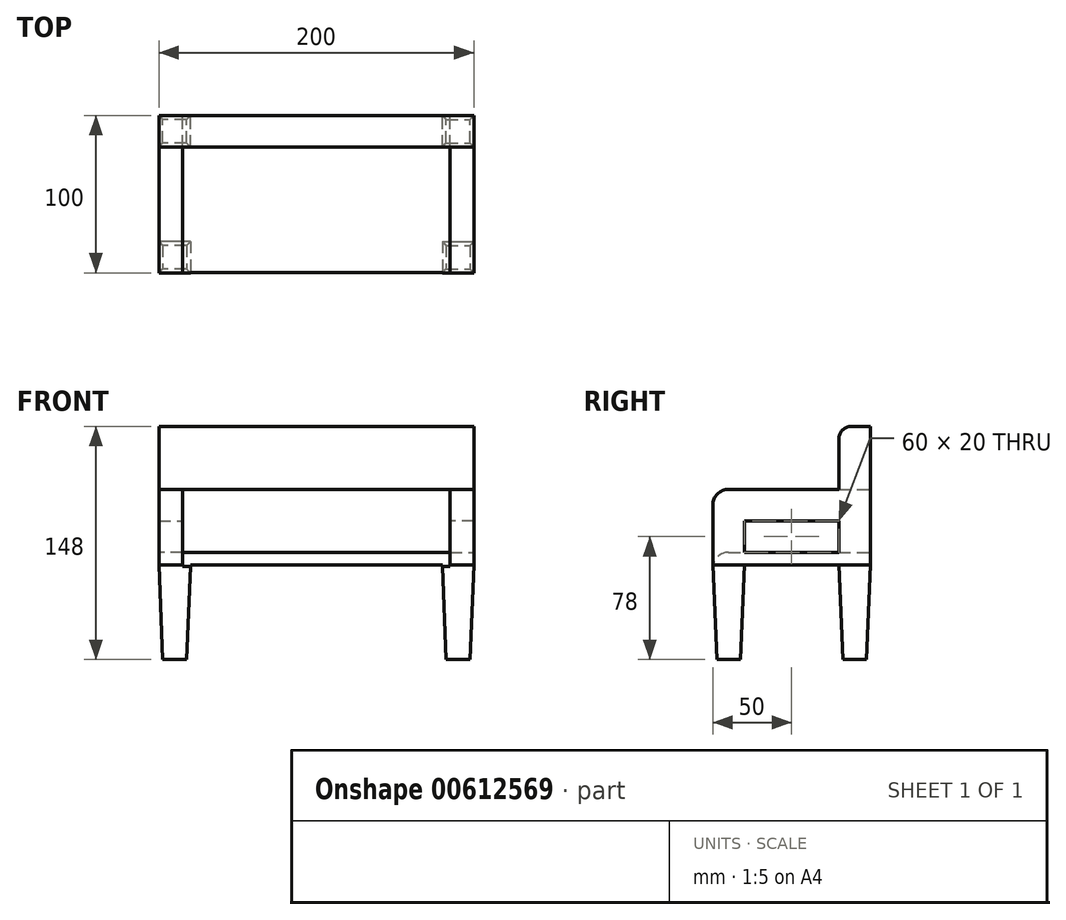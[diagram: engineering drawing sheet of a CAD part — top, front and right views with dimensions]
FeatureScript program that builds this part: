
annotation { "Feature Type Name" : "Feature", "Feature Type Description" : "" }
export const myFeature = defineFeature(function(context is Context, id is Id, definition is map)
    precondition{}
    {
        {
            var Q0;
            Q0=qCreatedBy(makeId("Top.planeOp"),FACE);
            var sketch = newSketch(context, id + "F0", { "sketchPlane" : qUnion([Q0])});
            skLineSegment(sketch, "E0.bottom", {"start": v(100, -50) * mm, "end": v(-100, -50) * mm});
            skLineSegment(sketch, "E0.top", {"start": v(100, 50) * mm, "end": v(-100, 50) * mm});
            skLineSegment(sketch, "E0.left", {"start": v(100, -50) * mm, "end": v(100, 50) * mm});
            skLineSegment(sketch, "E0.right", {"start": v(-100, -50) * mm, "end": v(-100, 50) * mm});
            skPoint(sketch, "E0.middle", {"position": v(0, 0) * mm});
            skSolve(sketch);
        }
        {
            var Q0;
            Q0=makeQuery(id+"F0.imprint","IMPRINT",FACE,{"disambiguationData":[TD([[makeQuery(id+"F0.imprint","IMPRINT",EDGE,{"derivedFrom":sQuery(id+"F0.wireOp",EDGE,"E0.bottom")}),-1.0]])]});
            extrude(context, id + "F1", {"entities" : qUnion([Q0]), "depth" : 8 * mm, "offsetDistance" : 25 * mm});
        }
        {
            var Q0;
            Q0=makeQuery(id+"F1.opExtrude","CAP_FACE",FACE,{"disambiguationData":[OSD([sQuery(id+"F0.wireOp",EDGE,"E0.bottom"),sQuery(id+"F0.wireOp",EDGE,"E0.top"),sQuery(id+"F0.wireOp",EDGE,"E0.left"),sQuery(id+"F0.wireOp",EDGE,"E0.right")])],"isStart":true});
            var sketch = newSketch(context, id + "F2", { "sketchPlane" : qUnion([Q0])});
            skPoint(sketch, "E1.middle", {"position": v(0, 0) * mm});
            skLineSegment(sketch, "E2.bottom", {"start": v(-80, 30) * mm, "end": v(-100, 30) * mm});
            skLineSegment(sketch, "E2.top", {"start": v(-80, 50) * mm, "end": v(-100, 50) * mm});
            skLineSegment(sketch, "E2.left", {"start": v(-80, 30) * mm, "end": v(-80, 50) * mm});
            skLineSegment(sketch, "E2.right", {"start": v(-100, 30) * mm, "end": v(-100, 50) * mm});
            skPoint(sketch, "E2.middle", {"position": v(-90, 40) * mm});
            skSolve(sketch);
        }
        {
            var Q0;
            Q0=qCreatedBy(makeId("Top.planeOp"),FACE);
            cPlane(context, id + "F3", {"entities" : qUnion([Q0]), "cplaneType" : CPlaneType.OFFSET, "offset" : 60 * mm, "oppositeDirection" : true, "width" : 150 * mm, "height" : 150 * mm});
        }
        {
            var Q0;
            Q0=qCreatedBy(id+"F3.planeOp",FACE);
            var sketch = newSketch(context, id + "F4", { "sketchPlane" : qUnion([Q0])});
            skLineSegment(sketch, "E3.bottom", {"start": v(-82.5, -32.5) * mm, "end": v(-97.5, -32.5) * mm});
            skLineSegment(sketch, "E3.top", {"start": v(-82.5, -47.5) * mm, "end": v(-97.5, -47.5) * mm});
            skLineSegment(sketch, "E3.left", {"start": v(-82.5, -32.5) * mm, "end": v(-82.5, -47.5) * mm});
            skLineSegment(sketch, "E3.right", {"start": v(-97.5, -32.5) * mm, "end": v(-97.5, -47.5) * mm});
            skPoint(sketch, "E3.middle", {"position": v(-90, -40) * mm});
            skSolve(sketch);
        }
        {
            var Q1;
            Q1=makeQuery(id+"F2.imprint","IMPRINT",FACE,{"disambiguationData":[TD([[makeQuery(id+"F2.imprint","IMPRINT",EDGE,{"derivedFrom":sQuery(id+"F2.wireOp",EDGE,"E2.bottom")}),-1.0]])]});
            var Q2;
            Q2=makeQuery(id+"F4.imprint","IMPRINT",FACE,{"disambiguationData":[TD([[makeQuery(id+"F4.imprint","IMPRINT",EDGE,{"derivedFrom":sQuery(id+"F4.wireOp",EDGE,"E3.bottom")}),1.0]])]});
            loft(context, id + "F5", {"operationType" : NewBodyOperationType.ADD, "sheetProfilesArray" : [{ "sheetProfileEntities" : qUnion([Q1]) }, { "sheetProfileEntities" : qUnion([Q2]) }]});
        }
        {
            var Q0;
            Q0=makeQuery(id+"F1.opExtrude","SWEPT_BODY",BODY,{"disambiguationData":[OSD([sQuery(id+"F0.wireOp",EDGE,"E0.bottom"),sQuery(id+"F0.wireOp",EDGE,"E0.top"),sQuery(id+"F0.wireOp",EDGE,"E0.left"),sQuery(id+"F0.wireOp",EDGE,"E0.right")])]});
            var Q1;
            Q1=qCreatedBy(makeId("Front.planeOp"),FACE);
            mirror(context, id + "F6", {"operationType" : NewBodyOperationType.ADD, "entities" : qUnion([Q0]), "mirrorPlane" : qUnion([Q1])});
        }
        {
            var Q0;
            Q0=makeQuery(id+"F1.opExtrude","SWEPT_BODY",BODY,{"disambiguationData":[OSD([sQuery(id+"F0.wireOp",EDGE,"E0.bottom"),sQuery(id+"F0.wireOp",EDGE,"E0.top"),sQuery(id+"F0.wireOp",EDGE,"E0.left"),sQuery(id+"F0.wireOp",EDGE,"E0.right")])]});
            var Q1;
            Q1=qCreatedBy(makeId("Right.planeOp"),FACE);
            mirror(context, id + "F7", {"operationType" : NewBodyOperationType.ADD, "entities" : qUnion([Q0]), "mirrorPlane" : qUnion([Q1])});
        }
        {
            var Q0;
            Q0=makeQuery(id+"F1.opExtrude","CAP_FACE",FACE,{"disambiguationData":[OSD([sQuery(id+"F0.wireOp",EDGE,"E0.bottom"),sQuery(id+"F0.wireOp",EDGE,"E0.top"),sQuery(id+"F0.wireOp",EDGE,"E0.left"),sQuery(id+"F0.wireOp",EDGE,"E0.right")])],"isStart":false});
            var sketch = newSketch(context, id + "F8", { "sketchPlane" : qUnion([Q0])});
            skLineSegment(sketch, "E4.bottom", {"start": v(-85, 30) * mm, "end": v(-100, 30) * mm});
            skLineSegment(sketch, "E4.top", {"start": v(-85, 50) * mm, "end": v(-100, 50) * mm});
            skLineSegment(sketch, "E4.left", {"start": v(-85, 30) * mm, "end": v(-85, 50) * mm});
            skLineSegment(sketch, "E4.right", {"start": v(-100, 30) * mm, "end": v(-100, 50) * mm});
            skPoint(sketch, "E4.middle", {"position": v(-92.5, 40) * mm});
            skSolve(sketch);
        }
        {
            var Q0;
            Q0=makeQuery(id+"F8.imprint","IMPRINT",FACE,{"disambiguationData":[TD([[makeQuery(id+"F8.imprint","IMPRINT",EDGE,{"derivedFrom":sQuery(id+"F8.wireOp",EDGE,"E4.bottom")}),-1.0]])]});
            extrude(context, id + "F9", {"entities" : qUnion([Q0]), "operationType" : NewBodyOperationType.ADD, "depth" : 80 * mm, "offsetDistance" : 25 * mm});
        }
        {
            var Q0;
            Q0=makeQuery(id+"F1.opExtrude","SWEPT_BODY",BODY,{"disambiguationData":[OSD([sQuery(id+"F0.wireOp",EDGE,"E0.bottom"),sQuery(id+"F0.wireOp",EDGE,"E0.top"),sQuery(id+"F0.wireOp",EDGE,"E0.left"),sQuery(id+"F0.wireOp",EDGE,"E0.right")])]});
            var Q1;
            Q1=qCreatedBy(makeId("Right.planeOp"),FACE);
            mirror(context, id + "F10", {"operationType" : NewBodyOperationType.ADD, "entities" : qUnion([Q0]), "mirrorPlane" : qUnion([Q1])});
        }
        {
            var Q0;
            Q0=makeQuery(id+"F9.opExtrude","SWEPT_FACE",FACE,{"disambiguationData":[OSD([sQuery(id+"F8.wireOp",EDGE,"E4.left")])]});
            var sketch = newSketch(context, id + "F11", { "sketchPlane" : qUnion([Q0])});
            skLineSegment(sketch, "E5.bottom", {"start": v(30, 48) * mm, "end": v(50, 48) * mm});
            skLineSegment(sketch, "E5.top", {"start": v(30, 88) * mm, "end": v(50, 88) * mm});
            skLineSegment(sketch, "E5.left", {"start": v(30, 48) * mm, "end": v(30, 88) * mm});
            skLineSegment(sketch, "E5.right", {"start": v(50, 48) * mm, "end": v(50, 88) * mm});
            skPoint(sketch, "E5.middle", {"position": v(40, 68) * mm});
            skSolve(sketch);
        }
        {
            var Q0;
            Q0=makeQuery(id+"F11.imprint","IMPRINT",FACE,{"disambiguationData":[TD([[makeQuery(id+"F11.imprint","IMPRINT",EDGE,{"derivedFrom":sQuery(id+"F11.wireOp",EDGE,"E5.bottom")}),1.0]])]});
            extrude(context, id + "F12", {"entities" : qUnion([Q0]), "operationType" : NewBodyOperationType.ADD, "depth" : 170 * mm, "offsetDistance" : 25 * mm});
        }
        {
            var Q0;
            {var subQ0=makeQuery(id+"F9.opExtrude","SWEPT_FACE",FACE,{"disambiguationData":[OSD([sQuery(id+"F8.wireOp",EDGE,"E4.bottom")])]});Q0=makeQuery(id+"F12.boolean.opBoolean","MERGE",FACE,{"derivedFrom":[subQ0,makeQuery(id+"F10.opPattern","COPY",FACE,{"derivedFrom":subQ0,"instanceName":"1"}),makeQuery(id+"F12.opExtrude","SWEPT_FACE",FACE,{"disambiguationData":[OSD([sQuery(id+"F11.wireOp",EDGE,"E5.left")])]})]});}
            var sketch = newSketch(context, id + "F13", { "sketchPlane" : qUnion([Q0])});
            skLineSegment(sketch, "E6", {"start": v(-85, 48) * mm, "end": v(-92.5, 48) * mm});
            skPoint(sketch, "E6.endSnap0", {"position": v(-100, 48) * mm});
            skLineSegment(sketch, "E7.bottom", {"start": v(-100, 28) * mm, "end": v(-85, 28) * mm});
            skLineSegment(sketch, "E7.top", {"start": v(-100, 48) * mm, "end": v(-85, 48) * mm});
            skLineSegment(sketch, "E7.left", {"start": v(-100, 28) * mm, "end": v(-100, 48) * mm});
            skLineSegment(sketch, "E7.right", {"start": v(-85, 28) * mm, "end": v(-85, 48) * mm});
            skPoint(sketch, "E7.middle", {"position": v(-92.5, 38) * mm});
            skSolve(sketch);
        }
        {
            var Q0;
            Q0=makeQuery(id+"F13.imprint","IMPRINT",FACE,{"disambiguationData":[TD([[makeQuery(id+"F13.imprint","IMPRINT",EDGE,{"derivedFrom":sQuery(id+"F13.wireOp",EDGE,"E7.bottom")}),1.0]])]});
            extrude(context, id + "F14", {"entities" : qUnion([Q0]), "operationType" : NewBodyOperationType.ADD, "depth" : 80 * mm, "offsetDistance" : 25 * mm});
        }
        {
            var Q0;
            Q0=makeQuery(id+"F14.opExtrude","SWEPT_FACE",FACE,{"disambiguationData":[OSD([sQuery(id+"F13.wireOp",EDGE,"E7.bottom")])]});
            var sketch = newSketch(context, id + "F15", { "sketchPlane" : qUnion([Q0])});
            skLineSegment(sketch, "E8.bottom", {"start": v(-85, 30) * mm, "end": v(-100, 30) * mm});
            skLineSegment(sketch, "E8.top", {"start": v(-85, 50) * mm, "end": v(-100, 50) * mm});
            skLineSegment(sketch, "E8.left", {"start": v(-85, 30) * mm, "end": v(-85, 50) * mm});
            skLineSegment(sketch, "E8.right", {"start": v(-100, 30) * mm, "end": v(-100, 50) * mm});
            skPoint(sketch, "E8.middle", {"position": v(-92.5, 40) * mm});
            skSolve(sketch);
        }
        {
            var Q0;
            Q0=makeQuery(id+"F15.imprint","IMPRINT",FACE,{"disambiguationData":[TD([[makeQuery(id+"F15.imprint","IMPRINT",EDGE,{"derivedFrom":sQuery(id+"F15.wireOp",EDGE,"E8.bottom")}),-1.0]])]});
            extrude(context, id + "F16", {"entities" : qUnion([Q0]), "operationType" : NewBodyOperationType.ADD, "depth" : 20 * mm, "offsetDistance" : 25 * mm});
        }
        {
            var Q0;
            Q0=makeQuery(id+"F1.opExtrude","SWEPT_BODY",BODY,{"disambiguationData":[OSD([sQuery(id+"F0.wireOp",EDGE,"E0.bottom"),sQuery(id+"F0.wireOp",EDGE,"E0.top"),sQuery(id+"F0.wireOp",EDGE,"E0.left"),sQuery(id+"F0.wireOp",EDGE,"E0.right")])]});
            var Q1;
            Q1=qCreatedBy(makeId("Right.planeOp"),FACE);
            mirror(context, id + "F17", {"operationType" : NewBodyOperationType.ADD, "entities" : qUnion([Q0]), "mirrorPlane" : qUnion([Q1])});
        }
        {
            var Q0;
            Q0=makeQuery(id+"F17.opPattern","COPY",EDGE,{"derivedFrom":makeQuery(id+"F14.opExtrude","CAP_EDGE",EDGE,{"disambiguationData":[OSD([sQuery(id+"F13.wireOp",EDGE,"E7.top")])],"isStart":false}),"instanceName":"1"});
            fillet(context, id + "F18", {"entities" : qUnion([Q0]), "radius" : 10 * mm, "tangentPropagation" : true, "allowEdgeOverflow" : false});
        }
        {
            var Q0;
            Q0=makeQuery(id+"F14.opExtrude","CAP_EDGE",EDGE,{"disambiguationData":[OSD([sQuery(id+"F13.wireOp",EDGE,"E7.top")])],"isStart":false});
            fillet(context, id + "F19", {"entities" : qUnion([Q0]), "radius" : 10 * mm, "tangentPropagation" : true, "allowEdgeOverflow" : false});
        }
        {
            var Q0;
            Q0=makeQuery(id+"F1.opExtrude","CAP_EDGE",EDGE,{"disambiguationData":[OSD([sQuery(id+"F0.wireOp",EDGE,"E0.bottom")])],"isStart":false});
            fillet(context, id + "F20", {"entities" : qUnion([Q0]), "radius" : 10 * mm, "tangentPropagation" : true, "allowEdgeOverflow" : false});
        }
        {
            var Q0;
            {var subQ0=makeQuery(id+"F9.opExtrude","CAP_EDGE",EDGE,{"disambiguationData":[OSD([sQuery(id+"F8.wireOp",EDGE,"E4.bottom")])],"isStart":false});Q0=makeQuery(id+"F12.boolean.opBoolean","MERGE",EDGE,{"derivedFrom":[subQ0,makeQuery(id+"F10.opPattern","COPY",EDGE,{"derivedFrom":subQ0,"instanceName":"1"}),makeQuery(id+"F12.opExtrude","SWEPT_EDGE",EDGE,{"disambiguationData":[OSD([sQuery(id+"F11.wireOp",EDGE,"E5.top"),sQuery(id+"F11.wireOp",EDGE,"E5.left")])]})]});}
            fillet(context, id + "F21", {"entities" : qUnion([Q0]), "radius" : 8 * mm, "tangentPropagation" : true, "allowEdgeOverflow" : false});
        }
    });
